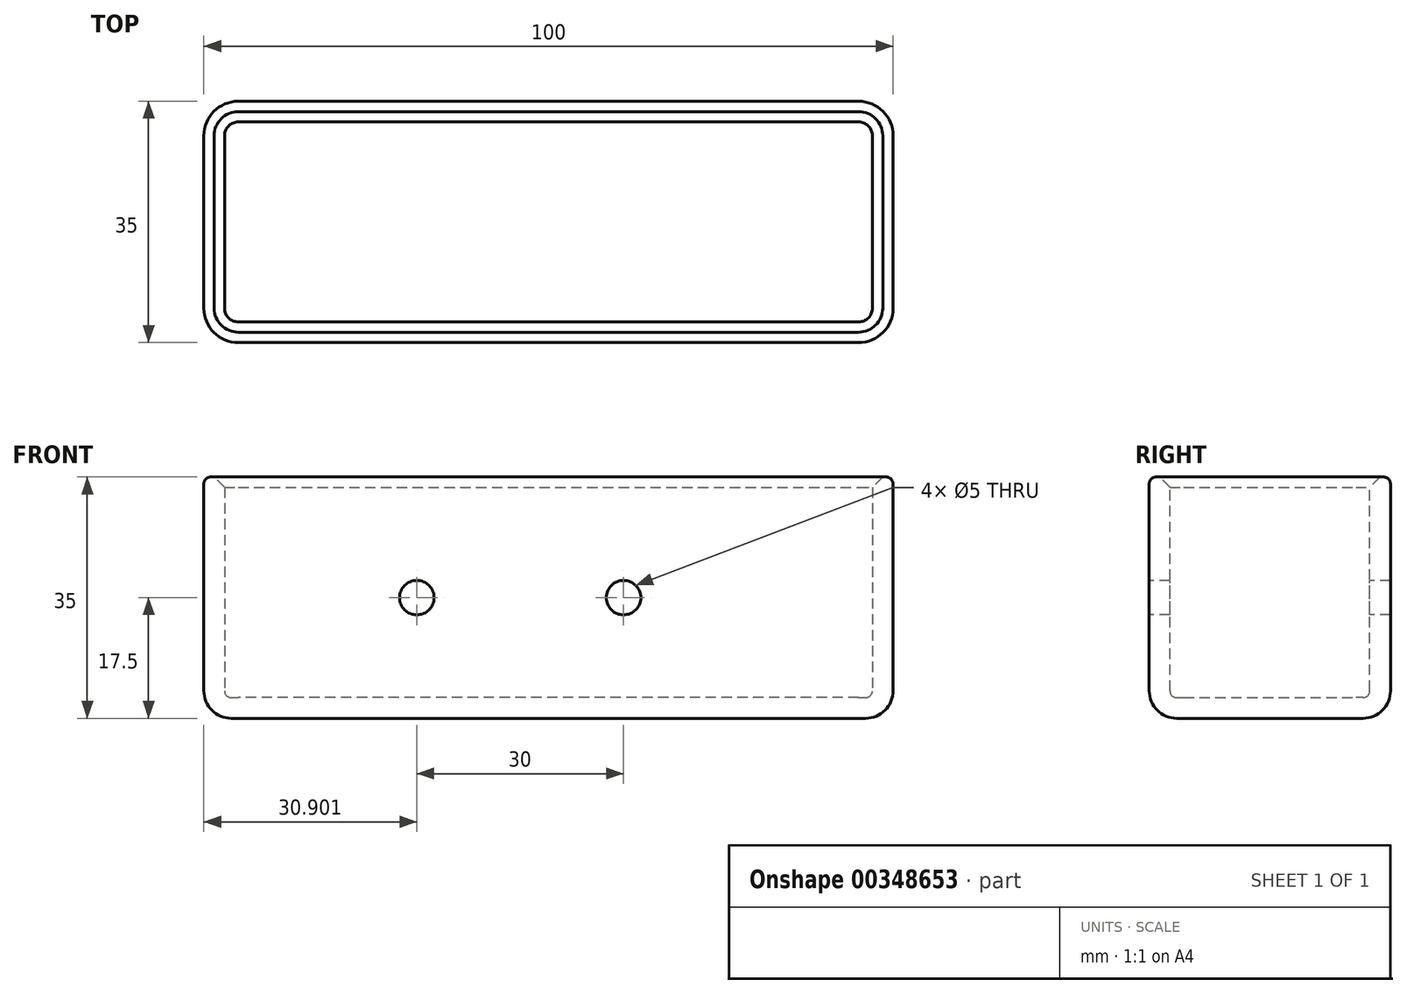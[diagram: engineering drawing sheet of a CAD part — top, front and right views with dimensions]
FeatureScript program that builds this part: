
annotation { "Feature Type Name" : "Feature", "Feature Type Description" : "" }
export const myFeature = defineFeature(function(context is Context, id is Id, definition is map)
    precondition{}
    {
        {
            var Q0;
            Q0=qCreatedBy(makeId("Front.planeOp"),FACE);
            var sketch = newSketch(context, id + "F0", { "sketchPlane" : qUnion([Q0])});
            skLineSegment(sketch, "E0.bottom", {"start": v(50, 17.5) * mm, "end": v(-50, 17.5) * mm});
            skLineSegment(sketch, "E0.top", {"start": v(50, -17.5) * mm, "end": v(-50, -17.5) * mm});
            skLineSegment(sketch, "E0.left", {"start": v(50, 17.5) * mm, "end": v(50, -17.5) * mm});
            skLineSegment(sketch, "E0.right", {"start": v(-50, 17.5) * mm, "end": v(-50, -17.5) * mm});
            skPoint(sketch, "E0.middle", {"position": v(0, 0) * mm});
            skSolve(sketch);
        }
        {
            var Q0;
            Q0=makeQuery(id+"F0.imprint","IMPRINT",FACE,{"disambiguationData":[TD([[makeQuery(id+"F0.imprint","IMPRINT",EDGE,{"derivedFrom":sQuery(id+"F0.wireOp",EDGE,"E0.bottom")}),1.0]])]});
            extrude(context, id + "F1", {"entities" : qUnion([Q0]), "depth" : 35 * mm});
        }
        {
            var Q0;
            Q0=makeQuery(id+"F1.opExtrude","CAP_EDGE",EDGE,{"disambiguationData":[OSD([sQuery(id+"F0.wireOp",EDGE,"E0.left")])],"isStart":false});
            var Q1;
            Q1=makeQuery(id+"F1.opExtrude","CAP_EDGE",EDGE,{"disambiguationData":[OSD([sQuery(id+"F0.wireOp",EDGE,"E0.left")])],"isStart":true});
            var Q2;
            Q2=makeQuery(id+"F1.opExtrude","CAP_EDGE",EDGE,{"disambiguationData":[OSD([sQuery(id+"F0.wireOp",EDGE,"E0.right")])],"isStart":false});
            var Q3;
            Q3=makeQuery(id+"F1.opExtrude","CAP_EDGE",EDGE,{"disambiguationData":[OSD([sQuery(id+"F0.wireOp",EDGE,"E0.right")])],"isStart":true});
            fillet(context, id + "F2", {"entities" : qUnion([Q0, Q1, Q2, Q3]), "radius" : 5 * mm, "tangentPropagation" : true, "allowEdgeOverflow" : false});
        }
        {
            var Q0;
            Q0=makeQuery(id+"F1.opExtrude","CAP_EDGE",EDGE,{"disambiguationData":[OSD([sQuery(id+"F0.wireOp",EDGE,"E0.top")])],"isStart":false});
            fillet(context, id + "F3", {"entities" : qUnion([Q0]), "radius" : 4 * mm, "tangentPropagation" : true, "allowEdgeOverflow" : false});
        }
        {
            var Q0;
            Q0=makeQuery(id+"F1.opExtrude","SWEPT_FACE",FACE,{"disambiguationData":[OSD([sQuery(id+"F0.wireOp",EDGE,"E0.bottom")])]});
            shell(context, id + "F4", {"entities" : qUnion([Q0]), "thickness" : 3 * mm});
        }
        {
            var Q0;
            Q0=makeQuery(id+"F1.opExtrude","CAP_FACE",FACE,{"disambiguationData":[OSD([sQuery(id+"F0.wireOp",EDGE,"E0.bottom"),sQuery(id+"F0.wireOp",EDGE,"E0.top"),sQuery(id+"F0.wireOp",EDGE,"E0.left"),sQuery(id+"F0.wireOp",EDGE,"E0.right")])],"isStart":false});
            var sketch = newSketch(context, id + "F5", { "sketchPlane" : qUnion([Q0])});
            skPoint(sketch, "E1", {"position": v(-19.1, 0) * mm});
            skPoint(sketch, "E2", {"position": v(10.9, 0) * mm});
            skSolve(sketch);
        }
        {
            var Q0;
            Q0=sQuery(id+"F5.wireOp",VERTEX,"E1");
            var Q1;
            Q1=sQuery(id+"F5.wireOp",VERTEX,"E2");
            var Q2;
            Q2=makeQuery(id+"F1.opExtrude","SWEPT_BODY",BODY,{"disambiguationData":[OSD([sQuery(id+"F0.wireOp",EDGE,"E0.bottom"),sQuery(id+"F0.wireOp",EDGE,"E0.top"),sQuery(id+"F0.wireOp",EDGE,"E0.left"),sQuery(id+"F0.wireOp",EDGE,"E0.right")])]});
            hole(context, id + "F6", {"style" : HoleStyle.SIMPLE, "endStyle" : HoleEndStyle.THROUGH, "standardTappedOrClearance" : lookupTablePath({ "standard" : "ISO", "size" : "5", "type" : "Drilled" }), "standardBlindInLast" : lookupTablePath({ "standard" : "ISO", "size" : "5", "type" : "Drilled" }), "holeDiameter" : 5 * mm, "isTappedThrough" : true, "tappedDepth" : 12.7 * mm, "tapClearance" : 3, "locations" : qUnion([Q0, Q1]), "scope" : qUnion([Q2])});
        }
        {
            var Q0;
            {var subQ0=sQuery(id+"F0.wireOp",EDGE,"E0.right");var subQ1=sQuery(id+"F0.wireOp",EDGE,"E0.bottom");Q0=makeQuery(id+"F4.opShell","OFFSET_EDGE",EDGE,{"disambiguationData":[OSD([subQ1,subQ0]),TDD([makeQuery(id+"F1.opExtrude","SWEPT_EDGE",EDGE,{"disambiguationData":[OSD([subQ1,subQ0])]})])]});}
            var Q1;
            {var subQ0=sQuery(id+"F0.wireOp",EDGE,"E0.bottom");var subQ1=sQuery(id+"F0.wireOp",EDGE,"E0.right");Q1=makeQuery(id+"F4.opShell","OFFSET_EDGE",EDGE,{"disambiguationData":[OSD([subQ0,subQ1]),TDD([makeQuery(id+"F2.opFillet","BLEND_EDGE",EDGE,{"blendedFrom":[makeQuery(id+"F1.opExtrude","CAP_EDGE",EDGE,{"disambiguationData":[OSD([subQ1])],"isStart":true}),makeQuery(id+"F1.opExtrude","SWEPT_FACE",FACE,{"disambiguationData":[OSD([subQ0])]})],"blendedInto":[makeQuery(id+"F1.opExtrude","SWEPT_FACE",FACE,{"disambiguationData":[OSD([subQ0])]})]})])]});}
            var Q2;
            {var subQ0=sQuery(id+"F0.wireOp",EDGE,"E0.bottom");Q2=makeQuery(id+"F4.opShell","OFFSET_EDGE",EDGE,{"disambiguationData":[OSD([subQ0]),TDD([makeQuery(id+"F1.opExtrude","CAP_EDGE",EDGE,{"disambiguationData":[OSD([subQ0])],"isStart":true})])]});}
            var Q3;
            {var subQ0=sQuery(id+"F0.wireOp",EDGE,"E0.bottom");var subQ1=sQuery(id+"F0.wireOp",EDGE,"E0.left");Q3=makeQuery(id+"F4.opShell","OFFSET_EDGE",EDGE,{"disambiguationData":[OSD([subQ0,subQ1]),TDD([makeQuery(id+"F2.opFillet","BLEND_EDGE",EDGE,{"blendedFrom":[makeQuery(id+"F1.opExtrude","CAP_EDGE",EDGE,{"disambiguationData":[OSD([subQ1])],"isStart":true}),makeQuery(id+"F1.opExtrude","SWEPT_FACE",FACE,{"disambiguationData":[OSD([subQ0])]})],"blendedInto":[makeQuery(id+"F1.opExtrude","SWEPT_FACE",FACE,{"disambiguationData":[OSD([subQ0])]})]})])]});}
            var Q4;
            {var subQ0=sQuery(id+"F0.wireOp",EDGE,"E0.left");var subQ1=sQuery(id+"F0.wireOp",EDGE,"E0.bottom");Q4=makeQuery(id+"F4.opShell","OFFSET_EDGE",EDGE,{"disambiguationData":[OSD([subQ1,subQ0]),TDD([makeQuery(id+"F1.opExtrude","SWEPT_EDGE",EDGE,{"disambiguationData":[OSD([subQ1,subQ0])]})])]});}
            var Q5;
            {var subQ0=sQuery(id+"F0.wireOp",EDGE,"E0.bottom");var subQ1=sQuery(id+"F0.wireOp",EDGE,"E0.left");Q5=makeQuery(id+"F4.opShell","OFFSET_EDGE",EDGE,{"disambiguationData":[OSD([subQ0,subQ1]),TDD([makeQuery(id+"F2.opFillet","BLEND_EDGE",EDGE,{"blendedFrom":[makeQuery(id+"F1.opExtrude","CAP_EDGE",EDGE,{"disambiguationData":[OSD([subQ1])],"isStart":false}),makeQuery(id+"F1.opExtrude","SWEPT_FACE",FACE,{"disambiguationData":[OSD([subQ0])]})],"blendedInto":[makeQuery(id+"F1.opExtrude","SWEPT_FACE",FACE,{"disambiguationData":[OSD([subQ0])]})]})])]});}
            var Q6;
            {var subQ0=sQuery(id+"F0.wireOp",EDGE,"E0.bottom");Q6=makeQuery(id+"F4.opShell","OFFSET_EDGE",EDGE,{"disambiguationData":[OSD([subQ0]),TDD([makeQuery(id+"F1.opExtrude","CAP_EDGE",EDGE,{"disambiguationData":[OSD([subQ0])],"isStart":false})])]});}
            var Q7;
            {var subQ0=sQuery(id+"F0.wireOp",EDGE,"E0.bottom");var subQ1=sQuery(id+"F0.wireOp",EDGE,"E0.right");Q7=makeQuery(id+"F4.opShell","OFFSET_EDGE",EDGE,{"disambiguationData":[OSD([subQ0,subQ1]),TDD([makeQuery(id+"F2.opFillet","BLEND_EDGE",EDGE,{"blendedFrom":[makeQuery(id+"F1.opExtrude","CAP_EDGE",EDGE,{"disambiguationData":[OSD([subQ1])],"isStart":false}),makeQuery(id+"F1.opExtrude","SWEPT_FACE",FACE,{"disambiguationData":[OSD([subQ0])]})],"blendedInto":[makeQuery(id+"F1.opExtrude","SWEPT_FACE",FACE,{"disambiguationData":[OSD([subQ0])]})]})])]});}
            chamfer(context, id + "F7", {"entities" : qUnion([Q0, Q1, Q2, Q3, Q4, Q5, Q6, Q7]), "width" : 1.5 * mm, "tangentPropagation" : true});
        }
        {
            var Q0;
            Q0=makeQuery(id+"F1.opExtrude","SWEPT_EDGE",EDGE,{"disambiguationData":[OSD([sQuery(id+"F0.wireOp",EDGE,"E0.bottom"),sQuery(id+"F0.wireOp",EDGE,"E0.right")])]});
            fillet(context, id + "F8", {"entities" : qUnion([Q0]), "radius" : 1 * mm, "tangentPropagation" : true, "allowEdgeOverflow" : false});
        }
    });
